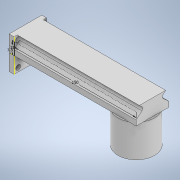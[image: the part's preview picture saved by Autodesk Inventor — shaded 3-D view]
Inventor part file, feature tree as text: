
AUTODESK INVENTOR PART (.ipt)
format: ipt  version: 2021.1 (Build 251245010, 245A)  size: 175,616 bytes
history: native  units: mm
features: sketch x6, extrude x5, plane x4, mirror x2
ambient origin geometry x8: Origin, YZ Plane, XZ Plane, XY Plane, X Axis, Y Axis, Z Axis, Center Point
bodies: Solid1 (feature_tree)
feature tree (17):
  extrude  "Extrusion1"  Depth=40.0mm
  extrude  "Extrusion2"  Depth=5.0mm
  mirror  "Mirror1"
  mirror  "Mirror2"
  plane  "Work Plane4"
  sketch  "Sketch3"  dims[d5=5.0mm d6=6.0mm]
  extrude  "Extrusion3"  Depth=6.0mm
  extrude  "Extrusion4"  [1 undecoded]
  extrude  "Extrusion5"  Depth=150.0mm
  sketch  "Sketch1"  dims[d0=40.0mm d1=40.0mm]
  sketch  "Sketch2"  dims[d2=6.0mm d3=0.0mm d4=5.0mm]
  plane  "Work Plane1"
  plane  "Work Plane2"
  plane  "Work Plane3"
  sketch  "Sketch4"  dims[d7=6.0mm d8=0.0mm d9=-20.0mm]
  sketch  "Sketch5"  dims[d10=15.0mm d11=150.0mm]
  sketch  "Sketch6"  dims[d12=7.5mm d13=150.0mm d14=0.0mm d15=10.0mm d16=60.0mm d17=40.0mm d18=45.0mm d19=40.0mm d20=0.0mm d21=38.0mm d22=25.0mm d23=0.0mm]
note: 1 required parameter value undecoded (feature->parameter linkage not recoverable at this tier; creation-order binding heuristic only, values carry confidence <= 0.55)
